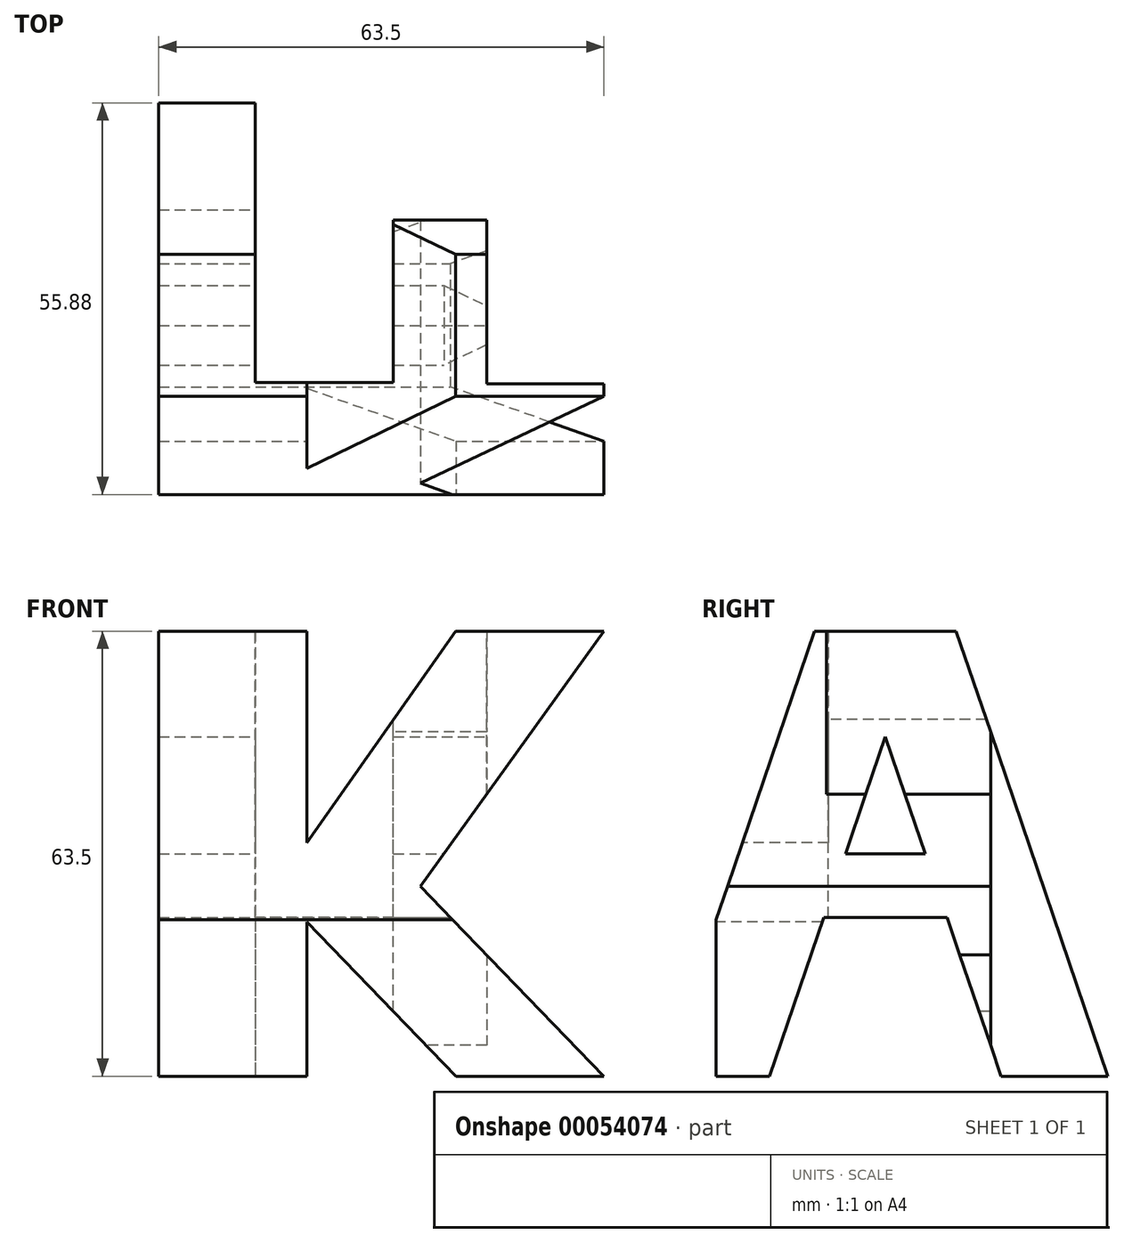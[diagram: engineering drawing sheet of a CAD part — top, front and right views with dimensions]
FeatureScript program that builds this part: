
annotation { "Feature Type Name" : "Feature", "Feature Type Description" : "" }
export const myFeature = defineFeature(function(context is Context, id is Id, definition is map)
    precondition{}
    {
        {
            var Q0;
            Q0=qCreatedBy(makeId("Front.planeOp"),FACE);
            var sketch = newSketch(context, id + "F0", { "sketchPlane" : qUnion([Q0])});
            skLineSegment(sketch, "E0", {"start": v(0, 0) * mm, "end": v(63.5, 0) * mm});
            skLineSegment(sketch, "E1", {"start": v(63.5, 0) * mm, "end": v(63.5, 63.5) * mm});
            skLineSegment(sketch, "E2", {"start": v(63.5, 63.5) * mm, "end": v(0, 63.5) * mm});
            skLineSegment(sketch, "E3", {"start": v(0, 63.5) * mm, "end": v(0, 0) * mm});
            skSolve(sketch);
        }
        {
            var Q0;
            Q0 = qSketchRegion(id + "F0", true);
            extrude(context, id + "F1", {"entities" : qUnion([Q0]), "depth" : 63.5 * mm});
        }
        {
            var Q0;
            Q0=qCreatedBy(makeId("Front.planeOp"),FACE);
            cPlane(context, id + "F2", {"entities" : qUnion([Q0]), "cplaneType" : CPlaneType.OFFSET, "offset" : 63.5 * mm, "width" : 152.4 * mm, "height" : 152.4 * mm});
        }
        {
            var Q0;
            Q0=qCreatedBy(makeId("Right.planeOp"),FACE);
            cPlane(context, id + "F3", {"entities" : qUnion([Q0]), "cplaneType" : CPlaneType.OFFSET, "offset" : 63.5 * mm, "width" : 152.4 * mm, "height" : 152.4 * mm});
        }
        {
            var Q0;
            Q0=qCreatedBy(makeId("Top.planeOp"),FACE);
            cPlane(context, id + "F4", {"entities" : qUnion([Q0]), "cplaneType" : CPlaneType.OFFSET, "offset" : 63.5 * mm, "width" : 152.4 * mm, "height" : 152.4 * mm});
        }
        {
            var Q0;
            Q0=qCreatedBy(id+"F3.planeOp",FACE);
            var sketch = newSketch(context, id + "F5", { "sketchPlane" : qUnion([Q0])});
            skLineSegment(sketch, "E4", {"start": v(0, 0) * mm, "end": v(-63.5, 0) * mm});
            skLineSegment(sketch, "E5", {"start": v(-63.5, 0) * mm, "end": v(-63.5, 63.5) * mm});
            skLineSegment(sketch, "E6", {"start": v(-63.5, 63.5) * mm, "end": v(0, 63.5) * mm});
            skLineSegment(sketch, "E7", {"start": v(0, 63.5) * mm, "end": v(0, 0) * mm});
            skLineSegment(sketch, "E8", {"start": v(-63.5, 0) * mm, "end": v(-41.86, 63.5) * mm});
            skLineSegment(sketch, "E9", {"start": v(-41.86, 63.5) * mm, "end": v(-21.64, 63.5) * mm});
            skLineSegment(sketch, "E10", {"start": v(-21.64, 63.5) * mm, "end": v(0, 0) * mm});
            skLineSegment(sketch, "E11", {"start": v(-37.44, 31.75) * mm, "end": v(-48.26, 0) * mm});
            skLineSegment(sketch, "E12", {"start": v(-37.44, 31.75) * mm, "end": v(-26.06, 31.75) * mm});
            skLineSegment(sketch, "E13", {"start": v(-26.06, 31.75) * mm, "end": v(-15.24, 0) * mm});
            skLineSegment(sketch, "E14", {"start": v(-37.44, 31.75) * mm, "end": v(-31.75, 48.44) * mm});
            skLineSegment(sketch, "E15", {"start": v(-31.75, 48.44) * mm, "end": v(-26.06, 31.75) * mm});
            skLineSegment(sketch, "E16", {"start": v(-40.54, 22.66) * mm, "end": v(-22.96, 22.66) * mm});
            skSolve(sketch);
        }
        {
            var Q0;
            {var subQ0=sQuery(id+"F5.wireOp",EDGE,"E5");Q0=makeQuery(id+"F5.imprint","IMPRINT",FACE,{"disambiguationData":[TD([[makeQuery(id+"F5.imprint","IMPRINT",EDGE,{"derivedFrom":subQ0}),-1.0]])]});}
            var Q1;
            Q1=makeQuery(id+"F5.imprint","IMPRINT",FACE,{"disambiguationData":[TD([[makeQuery(id+"F5.imprint","IMPRINT",EDGE,{"derivedFrom":sQuery(id+"F5.wireOp",EDGE,"E14")}),-1.0]])]});
            var Q2;
            {var subQ5=sQuery(id+"F5.wireOp",EDGE,"E16");Q2=makeQuery(id+"F5.imprint","IMPRINT",FACE,{"disambiguationData":[TD([[makeQuery(id+"F5.imprint","IMPRINT",EDGE,{"derivedFrom":subQ5}),-1.0]])]});}
            var Q3;
            {var subQ0=sQuery(id+"F5.wireOp",EDGE,"E7");Q3=makeQuery(id+"F5.imprint","IMPRINT",FACE,{"disambiguationData":[TD([[makeQuery(id+"F5.imprint","IMPRINT",EDGE,{"derivedFrom":subQ0}),-1.0]])]});}
            extrude(context, id + "F6", {"entities" : qUnion([Q0, Q1, Q2, Q3]), "operationType" : NewBodyOperationType.REMOVE, "oppositeDirection" : true, "depth" : 63.5 * mm});
        }
        {
            var Q0;
            Q0=qCreatedBy(id+"F2.planeOp",FACE);
            var sketch = newSketch(context, id + "F7", { "sketchPlane" : qUnion([Q0])});
            skLineSegment(sketch, "E17.bottom", {"start": v(0, 0) * mm, "end": v(63.5, 0) * mm});
            skLineSegment(sketch, "E17.top", {"start": v(0, 63.5) * mm, "end": v(63.5, 63.5) * mm});
            skLineSegment(sketch, "E17.left", {"start": v(0, 0) * mm, "end": v(0, 63.5) * mm});
            skLineSegment(sketch, "E17.right", {"start": v(63.5, 0) * mm, "end": v(63.5, 63.5) * mm});
            skLineSegment(sketch, "E18", {"start": v(0, 63.5) * mm, "end": v(0, 0) * mm});
            skLineSegment(sketch, "E19", {"start": v(40.62, 63.5) * mm, "end": v(54.4, 63.5) * mm});
            skLineSegment(sketch, "E20", {"start": v(48.5, 0) * mm, "end": v(63.5, 0) * mm});
            skLineSegment(sketch, "E21", {"start": v(63.5, 0) * mm, "end": v(37.31, 27.1) * mm});
            skLineSegment(sketch, "E22", {"start": v(37.31, 27.1) * mm, "end": v(63.5, 63.5) * mm});
            skLineSegment(sketch, "E23", {"start": v(21.16, 33.34) * mm, "end": v(21.16, 63.5) * mm});
            skLineSegment(sketch, "E24", {"start": v(21.16, 63.5) * mm, "end": v(0, 63.5) * mm});
            skLineSegment(sketch, "E25", {"start": v(0, 0) * mm, "end": v(21.16, 0) * mm});
            skLineSegment(sketch, "E26", {"start": v(21.16, 0) * mm, "end": v(21.16, 22) * mm});
            skLineSegment(sketch, "E27", {"start": v(21.16, 22) * mm, "end": v(42.42, 0) * mm});
            skLineSegment(sketch, "E28", {"start": v(21.16, 33.34) * mm, "end": v(42.34, 63.5) * mm});
            skSolve(sketch);
        }
        {
            var Q0;
            {var subQ0=sQuery(id+"F7.wireOp",EDGE,"E23");Q0=makeQuery(id+"F7.imprint","IMPRINT",FACE,{"disambiguationData":[TD([[makeQuery(id+"F7.imprint","IMPRINT",EDGE,{"derivedFrom":subQ0}),-1.0]])]});}
            var Q1;
            Q1=makeQuery(id+"F7.imprint","IMPRINT",FACE,{"disambiguationData":[TD([[makeQuery(id+"F7.imprint","IMPRINT",EDGE,{"derivedFrom":sQuery(id+"F7.wireOp",EDGE,"E17.right")}),1.0]])]});
            var Q2;
            {var subQ0=sQuery(id+"F7.wireOp",EDGE,"E26");Q2=makeQuery(id+"F7.imprint","IMPRINT",FACE,{"disambiguationData":[TD([[makeQuery(id+"F7.imprint","IMPRINT",EDGE,{"derivedFrom":subQ0}),-1.0]])]});}
            extrude(context, id + "F8", {"entities" : qUnion([Q0, Q1, Q2]), "operationType" : NewBodyOperationType.REMOVE, "oppositeDirection" : true, "depth" : 63.5 * mm});
        }
        {
            var Q0;
            Q0=qCreatedBy(id+"F4.planeOp",FACE);
            var sketch = newSketch(context, id + "F9", { "sketchPlane" : qUnion([Q0])});
            skLineSegment(sketch, "E29.bottom", {"start": v(0, 0) * mm, "end": v(63.5, 0) * mm});
            skLineSegment(sketch, "E29.top", {"start": v(0, -63.5) * mm, "end": v(63.5, -63.5) * mm});
            skLineSegment(sketch, "E29.left", {"start": v(0, 0) * mm, "end": v(0, -63.5) * mm});
            skLineSegment(sketch, "E29.right", {"start": v(63.5, 0) * mm, "end": v(63.5, -63.5) * mm});
            skLineSegment(sketch, "E30", {"start": v(63.5, -55.88) * mm, "end": v(0, -55.88) * mm});
            skLineSegment(sketch, "E31", {"start": v(0, -55.88) * mm, "end": v(0, 0) * mm});
            skLineSegment(sketch, "E32", {"start": v(0, 0) * mm, "end": v(13.79, 0) * mm});
            skLineSegment(sketch, "E33", {"start": v(13.79, 0) * mm, "end": v(13.79, -39.88) * mm});
            skLineSegment(sketch, "E34", {"start": v(13.79, -39.88) * mm, "end": v(33.48, -39.88) * mm});
            skLineSegment(sketch, "E35", {"start": v(33.48, -39.88) * mm, "end": v(33.48, -16.74) * mm});
            skLineSegment(sketch, "E36", {"start": v(33.48, -16.74) * mm, "end": v(46.78, -16.74) * mm});
            skLineSegment(sketch, "E37", {"start": v(46.78, -16.74) * mm, "end": v(46.78, -40.13) * mm});
            skLineSegment(sketch, "E38", {"start": v(46.78, -40.13) * mm, "end": v(63.5, -40.13) * mm});
            skSolve(sketch);
        }
        {
            var Q0;
            {var subQ1=sQuery(id+"F9.wireOp",EDGE,"E29.bottom");Q0=makeQuery(id+"F9.imprint","IMPRINT",FACE,{"disambiguationData":[TD([[makeQuery(id+"F9.imprint","IMPRINT",EDGE,{"derivedFrom":subQ1}),-1.0]])]});}
            var Q1;
            {var subQ0=sQuery(id+"F9.wireOp",EDGE,"E29.top");Q1=makeQuery(id+"F9.imprint","IMPRINT",FACE,{"disambiguationData":[TD([[makeQuery(id+"F9.imprint","IMPRINT",EDGE,{"derivedFrom":subQ0}),1.0]])]});}
            extrude(context, id + "F10", {"entities" : qUnion([Q0, Q1]), "operationType" : NewBodyOperationType.REMOVE, "oppositeDirection" : true, "depth" : 63.5 * mm});
        }
    });
